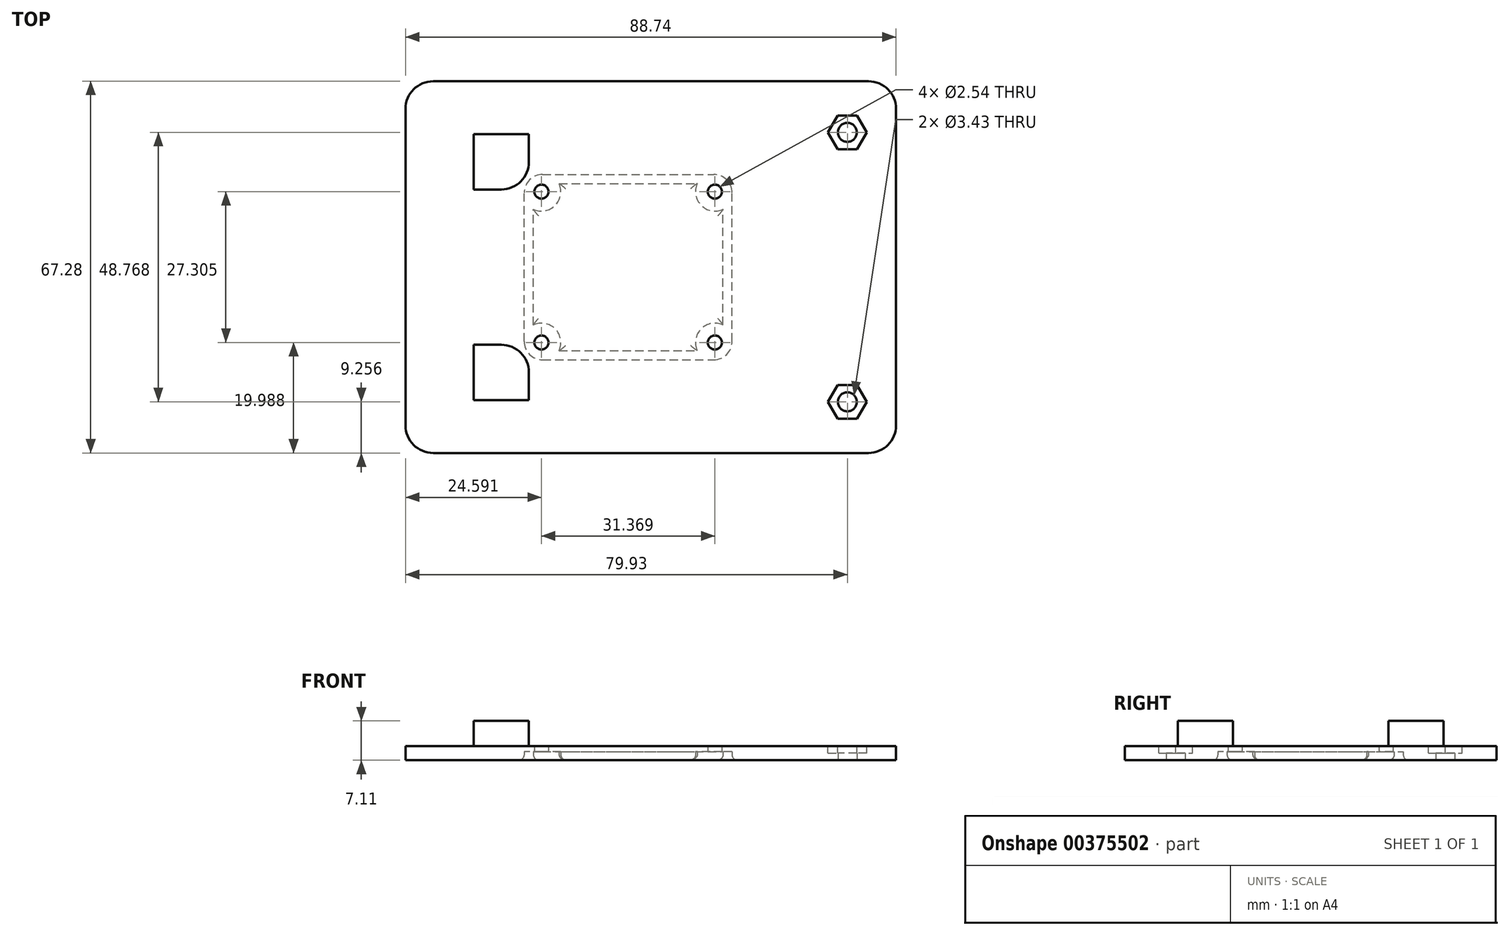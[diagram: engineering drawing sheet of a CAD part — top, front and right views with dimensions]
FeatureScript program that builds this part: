
annotation { "Feature Type Name" : "Feature", "Feature Type Description" : "" }
export const myFeature = defineFeature(function(context is Context, id is Id, definition is map)
    precondition{}
    {
        {
            var Q0;
            Q0=qCreatedBy(makeId("Top.planeOp"),FACE);
            var sketch = newSketch(context, id + "F0", { "sketchPlane" : qUnion([Q0])});
            skLineSegment(sketch, "E0.bottom", {"start": v(-39.37, 33.64) * mm, "end": v(39.37, 33.64) * mm});
            skLineSegment(sketch, "E0.top", {"start": v(-39.37, -33.64) * mm, "end": v(39.37, -33.64) * mm});
            skLineSegment(sketch, "E0.left", {"start": v(-44.37, 28.64) * mm, "end": v(-44.37, -28.64) * mm});
            skLineSegment(sketch, "E0.right", {"start": v(44.37, 28.64) * mm, "end": v(44.37, -28.64) * mm});
            skPoint(sketch, "E0.middle", {"position": v(0, 0) * mm});
            skPoint(sketch, "E1.visualSharp", {"position": v(-44.37, 33.64) * mm});
            skArc(sketch, "E1.filletArc", {"start": v(-39.37, 33.64) * mm, "mid": v(-42.9, 32.17) * mm, "end": v(-44.37, 28.64) * mm});
            skPoint(sketch, "E2.visualSharp", {"position": v(44.37, 33.64) * mm});
            skArc(sketch, "E2.filletArc", {"start": v(44.37, 28.64) * mm, "mid": v(42.9, 32.17) * mm, "end": v(39.37, 33.64) * mm});
            skPoint(sketch, "E3.visualSharp", {"position": v(44.37, -33.64) * mm});
            skArc(sketch, "E3.filletArc", {"start": v(39.37, -33.64) * mm, "mid": v(42.9, -32.17) * mm, "end": v(44.37, -28.64) * mm});
            skPoint(sketch, "E4.visualSharp", {"position": v(-44.37, -33.64) * mm});
            skArc(sketch, "E4.filletArc", {"start": v(-44.37, -28.64) * mm, "mid": v(-42.9, -32.17) * mm, "end": v(-39.37, -33.64) * mm});
            skCircle(sketch, "E5.cCircle", {"center": v(35.56, 24.38) * mm, "radius": 3.05 * mm, "construction": true});
            skLineSegment(sketch, "E5.0", {"start": v(37.32, 21.34) * mm, "end": v(33.8, 21.34) * mm});
            skLineSegment(sketch, "E5.1", {"start": v(33.8, 21.34) * mm, "end": v(32.04, 24.38) * mm});
            skLineSegment(sketch, "E5.2", {"start": v(32.04, 24.38) * mm, "end": v(33.8, 27.43) * mm});
            skLineSegment(sketch, "E5.3", {"start": v(33.8, 27.43) * mm, "end": v(37.32, 27.43) * mm});
            skLineSegment(sketch, "E5.4", {"start": v(37.32, 27.43) * mm, "end": v(39.08, 24.38) * mm});
            skLineSegment(sketch, "E5.5", {"start": v(39.08, 24.38) * mm, "end": v(37.32, 21.34) * mm});
            skPoint(sketch, "E5.0.midPoint", {"position": v(35.56, 21.34) * mm});
            skCircle(sketch, "E6.cCircle", {"center": v(35.56, -24.38) * mm, "radius": 3.05 * mm, "construction": true});
            skLineSegment(sketch, "E6.0", {"start": v(37.32, -27.43) * mm, "end": v(33.8, -27.43) * mm});
            skLineSegment(sketch, "E6.1", {"start": v(33.8, -27.43) * mm, "end": v(32.04, -24.38) * mm});
            skLineSegment(sketch, "E6.2", {"start": v(32.04, -24.38) * mm, "end": v(33.8, -21.34) * mm});
            skLineSegment(sketch, "E6.3", {"start": v(33.8, -21.34) * mm, "end": v(37.32, -21.34) * mm});
            skLineSegment(sketch, "E6.4", {"start": v(37.32, -21.34) * mm, "end": v(39.08, -24.38) * mm});
            skLineSegment(sketch, "E6.5", {"start": v(39.08, -24.38) * mm, "end": v(37.32, -27.43) * mm});
            skPoint(sketch, "E6.0.midPoint", {"position": v(35.56, -27.43) * mm});
            skLineSegment(sketch, "E7", {"start": v(35.56, 24.38) * mm, "end": v(35.56, -24.38) * mm, "construction": true});
            skPoint(sketch, "E8", {"position": v(35.56, 0) * mm});
            skPoint(sketch, "E9", {"position": v(44.37, 0) * mm});
            skCircle(sketch, "E10", {"center": v(35.56, 24.38) * mm, "radius": 1.71 * mm});
            skCircle(sketch, "E11", {"center": v(35.56, -24.38) * mm, "radius": 1.71 * mm});
            skLineSegment(sketch, "E12.bottom", {"start": v(-19.78, 13.65) * mm, "end": v(11.59, 13.65) * mm, "construction": true});
            skLineSegment(sketch, "E12.top", {"start": v(-19.78, -13.65) * mm, "end": v(11.59, -13.65) * mm, "construction": true});
            skLineSegment(sketch, "E12.left", {"start": v(-19.78, 13.65) * mm, "end": v(-19.78, -13.65) * mm, "construction": true});
            skLineSegment(sketch, "E12.right", {"start": v(11.59, 13.65) * mm, "end": v(11.59, -13.65) * mm, "construction": true});
            skPoint(sketch, "E12.middle", {"position": v(-4.1, 0) * mm});
            skCircle(sketch, "E13", {"center": v(-19.78, 13.65) * mm, "radius": 1.27 * mm});
            skCircle(sketch, "E14", {"center": v(-19.78, -13.65) * mm, "radius": 1.27 * mm});
            skCircle(sketch, "E15", {"center": v(11.59, 13.65) * mm, "radius": 1.27 * mm});
            skCircle(sketch, "E16", {"center": v(11.59, -13.65) * mm, "radius": 1.27 * mm});
            skSolve(sketch);
        }
        {
            var Q0;
            Q0 = qSketchRegion(id + "F0", true);
            var Q1;
            Q1=makeQuery(id+"F0.imprint","IMPRINT",FACE,{"disambiguationData":[TD([[makeQuery(id+"F0.imprint","IMPRINT",EDGE,{"derivedFrom":sQuery(id+"F0.wireOp",EDGE,"E5.0")}),-1.0]])]});
            var Q2;
            Q2=makeQuery(id+"F0.imprint","IMPRINT",FACE,{"disambiguationData":[TD([[makeQuery(id+"F0.imprint","IMPRINT",EDGE,{"derivedFrom":sQuery(id+"F0.wireOp",EDGE,"E6.0")}),-1.0]])]});
            extrude(context, id + "F1", {"entities" : qUnion([Q0, Q1, Q2]), "depth" : 2.54 * mm});
        }
        {
            var Q0;
            Q0=makeQuery(id+"F1.opExtrude","CAP_FACE",FACE,{"disambiguationData":[OSD([sQuery(id+"F0.wireOp",EDGE,"E0.bottom"),sQuery(id+"F0.wireOp",EDGE,"E0.top"),sQuery(id+"F0.wireOp",EDGE,"E0.left"),sQuery(id+"F0.wireOp",EDGE,"E0.right"),sQuery(id+"F0.wireOp",EDGE,"E1.filletArc"),sQuery(id+"F0.wireOp",EDGE,"E2.filletArc"),sQuery(id+"F0.wireOp",EDGE,"E3.filletArc"),sQuery(id+"F0.wireOp",EDGE,"E4.filletArc"),sQuery(id+"F0.wireOp",EDGE,"E10"),sQuery(id+"F0.wireOp",EDGE,"E11"),sQuery(id+"F0.wireOp",EDGE,"E13"),sQuery(id+"F0.wireOp",EDGE,"E14"),sQuery(id+"F0.wireOp",EDGE,"E15"),sQuery(id+"F0.wireOp",EDGE,"E16")])],"isStart":true});
            var sketch = newSketch(context, id + "F2", { "sketchPlane" : qUnion([Q0])});
            skLineSegment(sketch, "E17", {"start": v(-19.78, 13.65) * mm, "end": v(11.59, 13.65) * mm, "construction": true});
            skLineSegment(sketch, "E18", {"start": v(11.59, 13.65) * mm, "end": v(11.59, -13.65) * mm, "construction": true});
            skLineSegment(sketch, "E19.bottom", {"start": v(-19.59, 16.76) * mm, "end": v(11.4, 16.76) * mm});
            skLineSegment(sketch, "E19.top", {"start": v(-19.59, -16.76) * mm, "end": v(11.4, -16.76) * mm});
            skLineSegment(sketch, "E19.left", {"start": v(-22.9, 13.46) * mm, "end": v(-22.9, -13.46) * mm});
            skLineSegment(sketch, "E19.right", {"start": v(14.7, 13.46) * mm, "end": v(14.7, -13.46) * mm});
            skPoint(sketch, "E19.middle", {"position": v(-4.1, 0) * mm});
            skPoint(sketch, "E19.middle.positionSnap0", {"position": v(-4.1, 13.65) * mm});
            skPoint(sketch, "E19.centerSnap0", {"position": v(-4.1, 13.65) * mm});
            skPoint(sketch, "E20.visualSharp", {"position": v(-22.9, 16.76) * mm});
            skArc(sketch, "E20.filletArc", {"start": v(-19.59, 16.76) * mm, "mid": v(-21.92, 15.8) * mm, "end": v(-22.9, 13.46) * mm});
            skPoint(sketch, "E21.visualSharp", {"position": v(14.7, 16.76) * mm});
            skArc(sketch, "E21.filletArc", {"start": v(14.7, 13.46) * mm, "mid": v(13.73, 15.8) * mm, "end": v(11.4, 16.76) * mm});
            skPoint(sketch, "E22.visualSharp", {"position": v(14.7, -16.76) * mm});
            skArc(sketch, "E22.filletArc", {"start": v(11.4, -16.76) * mm, "mid": v(13.73, -15.8) * mm, "end": v(14.7, -13.46) * mm});
            skPoint(sketch, "E23.visualSharp", {"position": v(-22.9, -16.76) * mm});
            skArc(sketch, "E23.filletArc", {"start": v(-22.9, -13.46) * mm, "mid": v(-21.92, -15.8) * mm, "end": v(-19.59, -16.76) * mm});
            skLineSegment(sketch, "E24", {"start": v(-21.24, 10.47) * mm, "end": v(-21.24, -10.47) * mm});
            skLineSegment(sketch, "E25", {"start": v(-16.6, 15.11) * mm, "end": v(8.4, 15.11) * mm});
            skLineSegment(sketch, "E26", {"start": v(13.05, 10.47) * mm, "end": v(13.05, -10.47) * mm});
            skLineSegment(sketch, "E27", {"start": v(-16.6, -15.11) * mm, "end": v(8.4, -15.11) * mm});
            skArc(sketch, "E28", {"start": v(-16.6, -15.11) * mm, "mid": v(-17.3, -11.18) * mm, "end": v(-21.24, -10.47) * mm});
            skArc(sketch, "E29", {"start": v(13.05, -10.47) * mm, "mid": v(9.11, -11.18) * mm, "end": v(8.4, -15.11) * mm});
            skArc(sketch, "E30", {"start": v(8.4, 15.11) * mm, "mid": v(9.11, 11.18) * mm, "end": v(13.05, 10.47) * mm});
            skArc(sketch, "E31", {"start": v(-21.24, 10.47) * mm, "mid": v(-17.3, 11.18) * mm, "end": v(-16.6, 15.11) * mm});
            skLineSegment(sketch, "E32", {"start": v(-22.9, 0) * mm, "end": v(-21.24, 0) * mm, "construction": true});
            skLineSegment(sketch, "E33", {"start": v(-4.1, 16.76) * mm, "end": v(-4.1, 15.11) * mm, "construction": true});
            skLineSegment(sketch, "E34", {"start": v(14.7, 0) * mm, "end": v(13.05, 0) * mm, "construction": true});
            skLineSegment(sketch, "E35", {"start": v(-4.1, -16.76) * mm, "end": v(-4.1, -15.11) * mm, "construction": true});
            skSolve(sketch);
        }
        {
            var Q0;
            Q0 = qSketchRegion(id + "F2", true);
            extrude(context, id + "F3", {"entities" : qUnion([Q0]), "operationType" : NewBodyOperationType.REMOVE, "oppositeDirection" : true, "depth" : 1.52 * mm});
        }
        {
            var Q0;
            Q0=makeQuery(id+"F3.boolean.opBoolean","SPLIT",FACE,{"disambiguationData":[TD([makeQuery(id+"F3.opExtrude","SWEPT_FACE",FACE,{"disambiguationData":[OSD([sQuery(id+"F2.wireOp",EDGE,"E24")])]})])],"derivedFrom":makeQuery(id+"F1.opExtrude","CAP_FACE",FACE,{"disambiguationData":[OSD([sQuery(id+"F0.wireOp",EDGE,"E0.bottom"),sQuery(id+"F0.wireOp",EDGE,"E0.top"),sQuery(id+"F0.wireOp",EDGE,"E0.left"),sQuery(id+"F0.wireOp",EDGE,"E0.right"),sQuery(id+"F0.wireOp",EDGE,"E1.filletArc"),sQuery(id+"F0.wireOp",EDGE,"E2.filletArc"),sQuery(id+"F0.wireOp",EDGE,"E3.filletArc"),sQuery(id+"F0.wireOp",EDGE,"E4.filletArc"),sQuery(id+"F0.wireOp",EDGE,"E10"),sQuery(id+"F0.wireOp",EDGE,"E11"),sQuery(id+"F0.wireOp",EDGE,"E13"),sQuery(id+"F0.wireOp",EDGE,"E14"),sQuery(id+"F0.wireOp",EDGE,"E15"),sQuery(id+"F0.wireOp",EDGE,"E16")])],"isStart":true})});
            var Q1;
            Q1=makeQuery(id+"F3.boolean.opBoolean","COPY",EDGE,{"derivedFrom":makeQuery(id+"F3.opExtrude","CAP_EDGE",EDGE,{"disambiguationData":[OSD([sQuery(id+"F2.wireOp",EDGE,"E19.left")])],"isStart":true})});
            var Q2;
            Q2=makeQuery(id+"F3.boolean.opBoolean","COPY",EDGE,{"derivedFrom":makeQuery(id+"F3.opExtrude","CAP_EDGE",EDGE,{"disambiguationData":[OSD([sQuery(id+"F2.wireOp",EDGE,"E20.filletArc")])],"isStart":true})});
            fillet(context, id + "F4", {"entities" : qUnion([Q0, Q1, Q2]), "radius" : 1 * mm, "tangentPropagation" : true, "allowEdgeOverflow" : false});
        }
        {
            var Q0;
            Q0=makeQuery(id+"F1.opExtrude","CAP_FACE",FACE,{"disambiguationData":[OSD([sQuery(id+"F0.wireOp",EDGE,"E0.bottom"),sQuery(id+"F0.wireOp",EDGE,"E0.top"),sQuery(id+"F0.wireOp",EDGE,"E0.left"),sQuery(id+"F0.wireOp",EDGE,"E0.right"),sQuery(id+"F0.wireOp",EDGE,"E1.filletArc"),sQuery(id+"F0.wireOp",EDGE,"E2.filletArc"),sQuery(id+"F0.wireOp",EDGE,"E3.filletArc"),sQuery(id+"F0.wireOp",EDGE,"E4.filletArc"),sQuery(id+"F0.wireOp",EDGE,"E10"),sQuery(id+"F0.wireOp",EDGE,"E11"),sQuery(id+"F0.wireOp",EDGE,"E13"),sQuery(id+"F0.wireOp",EDGE,"E14"),sQuery(id+"F0.wireOp",EDGE,"E15"),sQuery(id+"F0.wireOp",EDGE,"E16")])],"isStart":false});
            var sketch = newSketch(context, id + "F5", { "sketchPlane" : qUnion([Q0])});
            skCircle(sketch, "E36.cCircle", {"center": v(35.56, 24.38) * mm, "radius": 3.05 * mm, "construction": true});
            skLineSegment(sketch, "E36.0", {"start": v(32.04, 24.38) * mm, "end": v(33.8, 27.43) * mm});
            skLineSegment(sketch, "E36.1", {"start": v(33.8, 27.43) * mm, "end": v(37.32, 27.43) * mm});
            skLineSegment(sketch, "E36.2", {"start": v(37.32, 27.43) * mm, "end": v(39.08, 24.38) * mm});
            skLineSegment(sketch, "E36.3", {"start": v(39.08, 24.38) * mm, "end": v(37.32, 21.34) * mm});
            skLineSegment(sketch, "E36.4", {"start": v(37.32, 21.34) * mm, "end": v(33.8, 21.34) * mm});
            skLineSegment(sketch, "E36.5", {"start": v(33.8, 21.34) * mm, "end": v(32.04, 24.38) * mm});
            skPoint(sketch, "E36.0.midPoint", {"position": v(32.92, 25.9) * mm});
            skCircle(sketch, "E37.cCircle", {"center": v(35.56, -24.38) * mm, "radius": 3.05 * mm, "construction": true});
            skLineSegment(sketch, "E37.0", {"start": v(32.04, -24.38) * mm, "end": v(33.8, -21.34) * mm});
            skLineSegment(sketch, "E37.1", {"start": v(33.8, -21.34) * mm, "end": v(37.32, -21.34) * mm});
            skLineSegment(sketch, "E37.2", {"start": v(37.32, -21.34) * mm, "end": v(39.08, -24.38) * mm});
            skLineSegment(sketch, "E37.3", {"start": v(39.08, -24.38) * mm, "end": v(37.32, -27.43) * mm});
            skLineSegment(sketch, "E37.4", {"start": v(37.32, -27.43) * mm, "end": v(33.8, -27.43) * mm});
            skLineSegment(sketch, "E37.5", {"start": v(33.8, -27.43) * mm, "end": v(32.04, -24.38) * mm});
            skPoint(sketch, "E37.0.midPoint", {"position": v(32.92, -22.86) * mm});
            skSolve(sketch);
        }
        {
            var Q0;
            Q0 = qSketchRegion(id + "F5", true);
            extrude(context, id + "F6", {"entities" : qUnion([Q0]), "operationType" : NewBodyOperationType.REMOVE, "oppositeDirection" : true, "depth" : 1.27 * mm});
        }
        {
            var Q0;
            Q0=makeQuery(id+"F1.opExtrude","CAP_FACE",FACE,{"disambiguationData":[OSD([sQuery(id+"F0.wireOp",EDGE,"E0.bottom"),sQuery(id+"F0.wireOp",EDGE,"E0.top"),sQuery(id+"F0.wireOp",EDGE,"E0.left"),sQuery(id+"F0.wireOp",EDGE,"E0.right"),sQuery(id+"F0.wireOp",EDGE,"E1.filletArc"),sQuery(id+"F0.wireOp",EDGE,"E2.filletArc"),sQuery(id+"F0.wireOp",EDGE,"E3.filletArc"),sQuery(id+"F0.wireOp",EDGE,"E4.filletArc"),sQuery(id+"F0.wireOp",EDGE,"E10"),sQuery(id+"F0.wireOp",EDGE,"E11"),sQuery(id+"F0.wireOp",EDGE,"E13"),sQuery(id+"F0.wireOp",EDGE,"E14"),sQuery(id+"F0.wireOp",EDGE,"E15"),sQuery(id+"F0.wireOp",EDGE,"E16")])],"isStart":false});
            var sketch = newSketch(context, id + "F7", { "sketchPlane" : qUnion([Q0])});
            skPoint(sketch, "E38.firstSnap0", {"position": v(35.56, 21.34) * mm});
            skLineSegment(sketch, "E38.left", {"start": v(35.56, -24.38) * mm, "end": v(35.56, 24.38) * mm, "construction": true});
            skPoint(sketch, "E39.middle", {"position": v(-27.05, 19.05) * mm});
            skPoint(sketch, "E40.middle", {"position": v(-27.05, -19.05) * mm});
            skLineSegment(sketch, "E41.bottom", {"start": v(-22.05, 24.05) * mm, "end": v(-32.05, 24.05) * mm});
            skLineSegment(sketch, "E41.top", {"start": v(-22.05, 14.05) * mm, "end": v(-32.05, 14.05) * mm});
            skLineSegment(sketch, "E41.left", {"start": v(-22.05, 24.05) * mm, "end": v(-22.05, 14.05) * mm});
            skLineSegment(sketch, "E41.right", {"start": v(-32.05, 24.05) * mm, "end": v(-32.05, 14.05) * mm});
            skLineSegment(sketch, "E42.bottom", {"start": v(-22.05, -24.05) * mm, "end": v(-32.05, -24.05) * mm});
            skLineSegment(sketch, "E42.top", {"start": v(-22.05, -14.05) * mm, "end": v(-32.05, -14.05) * mm});
            skLineSegment(sketch, "E42.left", {"start": v(-22.05, -24.05) * mm, "end": v(-22.05, -14.05) * mm});
            skLineSegment(sketch, "E42.right", {"start": v(-32.05, -24.05) * mm, "end": v(-32.05, -14.05) * mm});
            skLineSegment(sketch, "E43", {"start": v(-27.05, 19.05) * mm, "end": v(-27.05, -19.05) * mm, "construction": true});
            skLineSegment(sketch, "E44", {"start": v(-27.05, 19.05) * mm, "end": v(35.56, 19.05) * mm, "construction": true});
            skLineSegment(sketch, "E45", {"start": v(-27.05, -19.05) * mm, "end": v(35.56, -19.05) * mm, "construction": true});
            skPoint(sketch, "E46", {"position": v(-27.05, 0) * mm});
            skSolve(sketch);
        }
        {
            var Q0;
            Q0 = qSketchRegion(id + "F7", true);
            extrude(context, id + "F8", {"entities" : qUnion([Q0]), "operationType" : NewBodyOperationType.ADD, "depth" : 4.57 * mm});
        }
        {
            var Q0;
            Q0=makeQuery(id+"F8.opExtrude","SWEPT_EDGE",EDGE,{"disambiguationData":[OSD([sQuery(id+"F7.wireOp",EDGE,"E42.top"),sQuery(id+"F7.wireOp",EDGE,"E42.left")])]});
            var Q1;
            Q1=makeQuery(id+"F8.opExtrude","SWEPT_EDGE",EDGE,{"disambiguationData":[OSD([sQuery(id+"F7.wireOp",EDGE,"E41.top"),sQuery(id+"F7.wireOp",EDGE,"E41.left")])]});
            fillet(context, id + "F9", {"entities" : qUnion([Q0, Q1]), "radius" : 5 * mm, "tangentPropagation" : true, "allowEdgeOverflow" : false});
        }
    });
